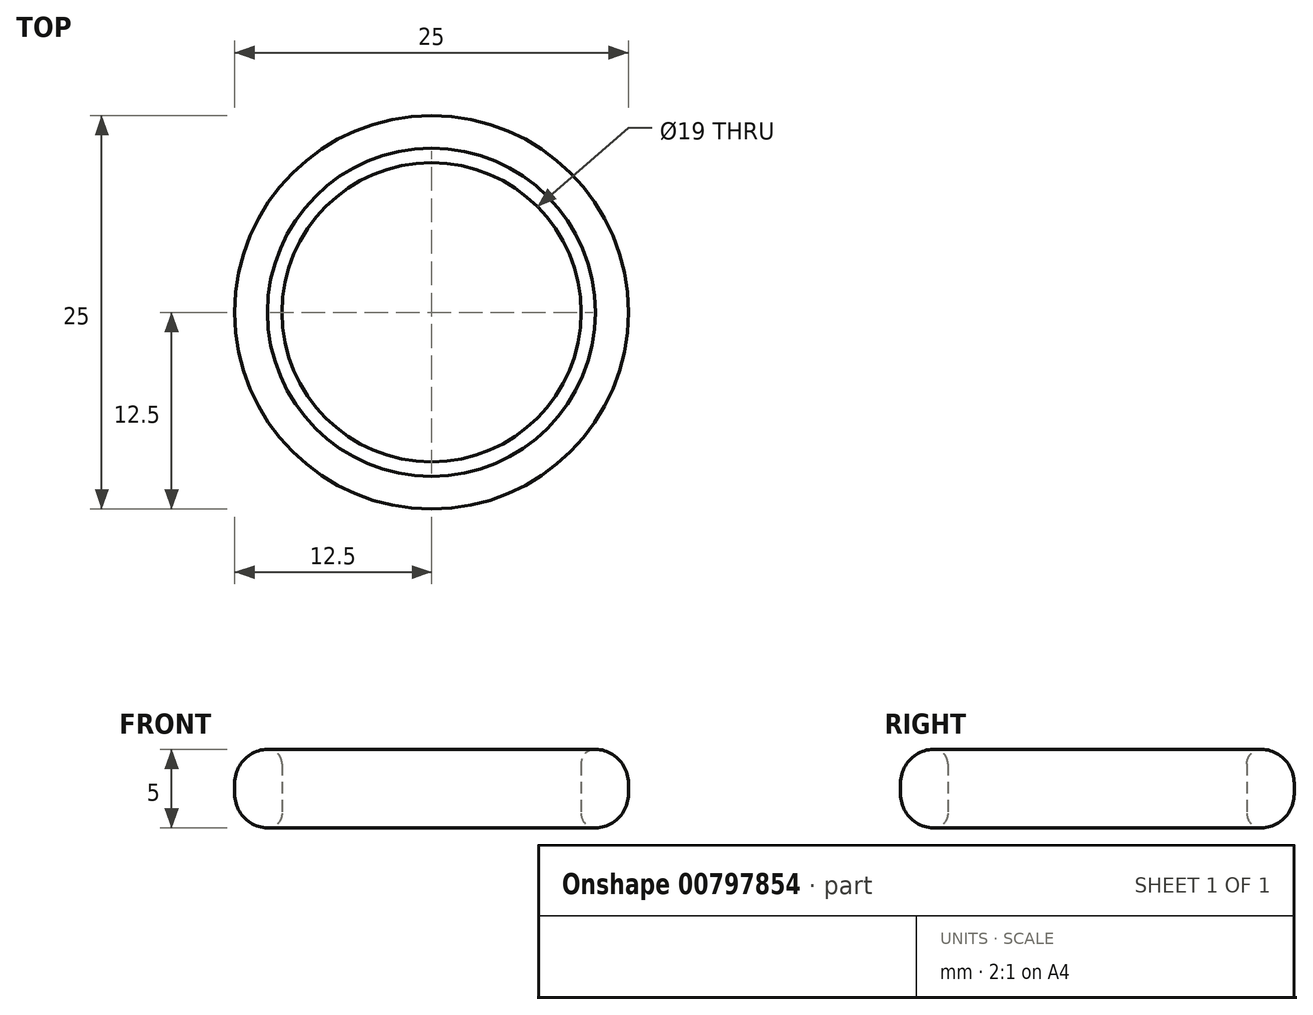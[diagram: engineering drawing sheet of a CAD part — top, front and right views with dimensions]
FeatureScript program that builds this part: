
annotation { "Feature Type Name" : "Feature", "Feature Type Description" : "" }
export const myFeature = defineFeature(function(context is Context, id is Id, definition is map)
    precondition{}
    {
        {
            var Q0;
            Q0=qCreatedBy(makeId("Top.planeOp"),FACE);
            var sketch = newSketch(context, id + "F0", { "sketchPlane" : qUnion([Q0])});
            skCircle(sketch, "E0", {"center": v(0, 0) * mm, "radius": 12.5 * mm});
            skCircle(sketch, "E1", {"center": v(0, 0) * mm, "radius": 9.5 * mm});
            skSolve(sketch);
        }
        {
            var Q0;
            Q0 = qSketchRegion(id + "F0", true);
            extrude(context, id + "F1", {"entities" : qUnion([Q0]), "depth" : 5 * mm, "offsetDistance" : 25.4 * mm});
        }
        {
            var Q0;
            Q0=makeQuery(id+"F1.opExtrude","CAP_EDGE",EDGE,{"disambiguationData":[OSD([sQuery(id+"F0.wireOp",EDGE,"E1")])],"isStart":false});
            var Q1;
            Q1=makeQuery(id+"F1.opExtrude","CAP_EDGE",EDGE,{"disambiguationData":[OSD([sQuery(id+"F0.wireOp",EDGE,"E1")])],"isStart":true});
            fillet(context, id + "F2", {"entities" : qUnion([Q0, Q1]), "radius" : 0.92 * mm, "tangentPropagation" : true, "allowEdgeOverflow" : false});
        }
        {
            var Q0;
            Q0=makeQuery(id+"F1.opExtrude","CAP_EDGE",EDGE,{"disambiguationData":[OSD([sQuery(id+"F0.wireOp",EDGE,"E0")])],"isStart":true});
            var Q1;
            Q1=makeQuery(id+"F1.opExtrude","CAP_EDGE",EDGE,{"disambiguationData":[OSD([sQuery(id+"F0.wireOp",EDGE,"E0")])],"isStart":false});
            fillet(context, id + "F3", {"entities" : qUnion([Q0, Q1]), "radius" : 2.15 * mm, "tangentPropagation" : true, "allowEdgeOverflow" : false});
        }
    });
